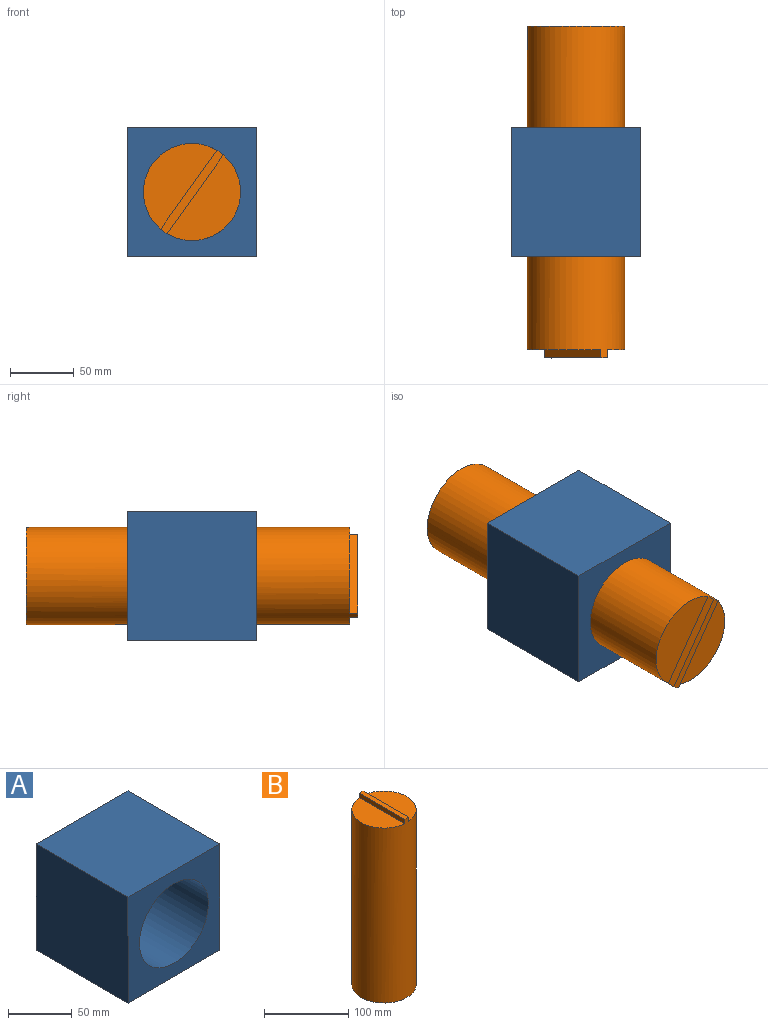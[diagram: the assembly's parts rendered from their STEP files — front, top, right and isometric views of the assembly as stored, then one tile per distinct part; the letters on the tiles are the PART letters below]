
ASSEMBLY  parts=2 mates=1
PART A: 7 faces, bbox 101.6x101.6x101.6 mm
  f0: plane 101.6x101.6mm, normal (-1,0,0), area 10322.6mm2, adj f1,f3,f5,f6
  f1: plane 101.6x101.6mm, normal (0,0,-1), area 10322.6mm2, adj f0,f2,f5,f6
  f2: plane 101.6x101.6mm, normal (1,0,0), area 10322.6mm2, adj f1,f3,f5,f6
  f3: plane 101.6x101.6mm, normal (0,0,1), area 10322.6mm2, adj f0,f2,f5,f6
  f4: cylinder r=38.1mm len=101.6mm, axis (0,1,0), area 24322mm2, adj f5,f6
  f5: plane 101.6x101.6mm, normal (0,-1,0), area 5762.2mm2, adj f0,f1,f2,f3,f4
  f6: plane 101.6x101.6mm, normal (0,1,0), area 5762.2mm2, adj f0,f1,f2,f3,f4
PART B: 7 faces, bbox 76.2x76.2x260.4 mm
  f0: plane 75.94x34.93mm, normal (0,0,1), area 2038.5mm2, adj f1,f5
  f1: cylinder r=38.1mm len=260.35mm, axis (0,0,-1), area 60885.6mm2, adj f0,f2,f3,f4,f5,f6
  f2: plane 75.94x34.93mm, normal (0,0,1), area 2038.5mm2, adj f1,f4
  f3: plane 76.2x76.2mm, normal (0,0,-1), area 4560.4mm2, adj f1
  f4: plane 75.94x6.35mm, normal (-1,0,0), area 482.2mm2, adj f1,f2,f6
  f5: plane 75.94x6.35mm, normal (1,0,0), area 482.2mm2, adj f0,f1,f6
  f6: plane 76.2x6.35mm, normal (0,0,1), area 483.3mm2, adj f1,f4,f5
PLACE A t=(-50.8,50.8,0)mm
PLACE B rot(axis=(0.91,0.29,-0.29),95.3deg) t=(0,130.18,50.8)mm
MATE revolute B.f1 <-> A.f4  axis (0,1,0) through (0,0,50.8)mm
